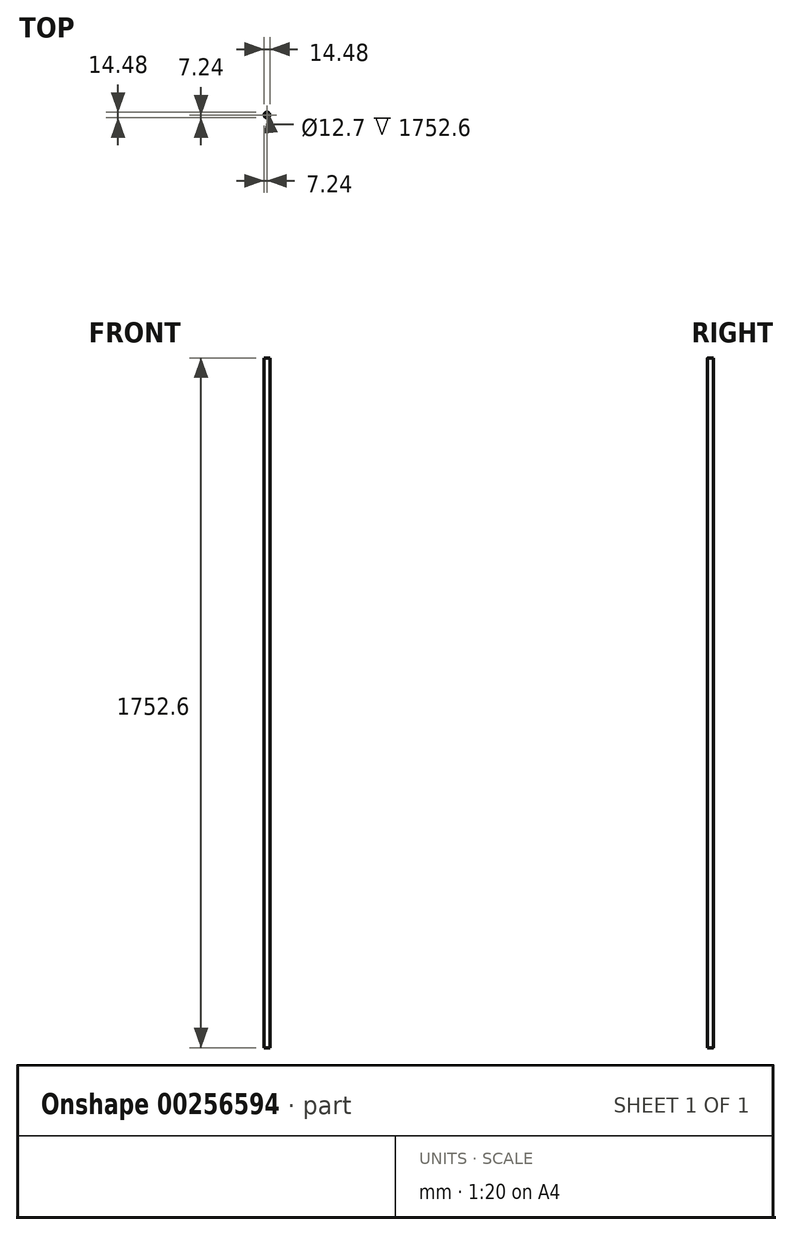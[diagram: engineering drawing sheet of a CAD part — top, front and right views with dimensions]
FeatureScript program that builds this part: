
annotation { "Feature Type Name" : "Feature", "Feature Type Description" : "" }
export const myFeature = defineFeature(function(context is Context, id is Id, definition is map)
    precondition{}
    {
        {
            var Q0;
            Q0=qCreatedBy(makeId("Top.planeOp"),FACE);
            var sketch = newSketch(context, id + "F0", { "sketchPlane" : qUnion([Q0])});
            skCircle(sketch, "E0", {"center": v(0, 0) * mm, "radius": 7.24 * mm});
            skCircle(sketch, "E1", {"center": v(0, 0) * mm, "radius": 6.35 * mm});
            skSolve(sketch);
        }
        {
            var Q0;
            Q0=makeQuery(id+"F0.imprint","IMPRINT",FACE,{"disambiguationData":[TD([[makeQuery(id+"F0.imprint","IMPRINT",EDGE,{"derivedFrom":sQuery(id+"F0.wireOp",EDGE,"E0")}),1.0]])]});
            extrude(context, id + "F1", {"entities" : qUnion([Q0]), "depth" : 1752.6 * mm});
        }
    });
